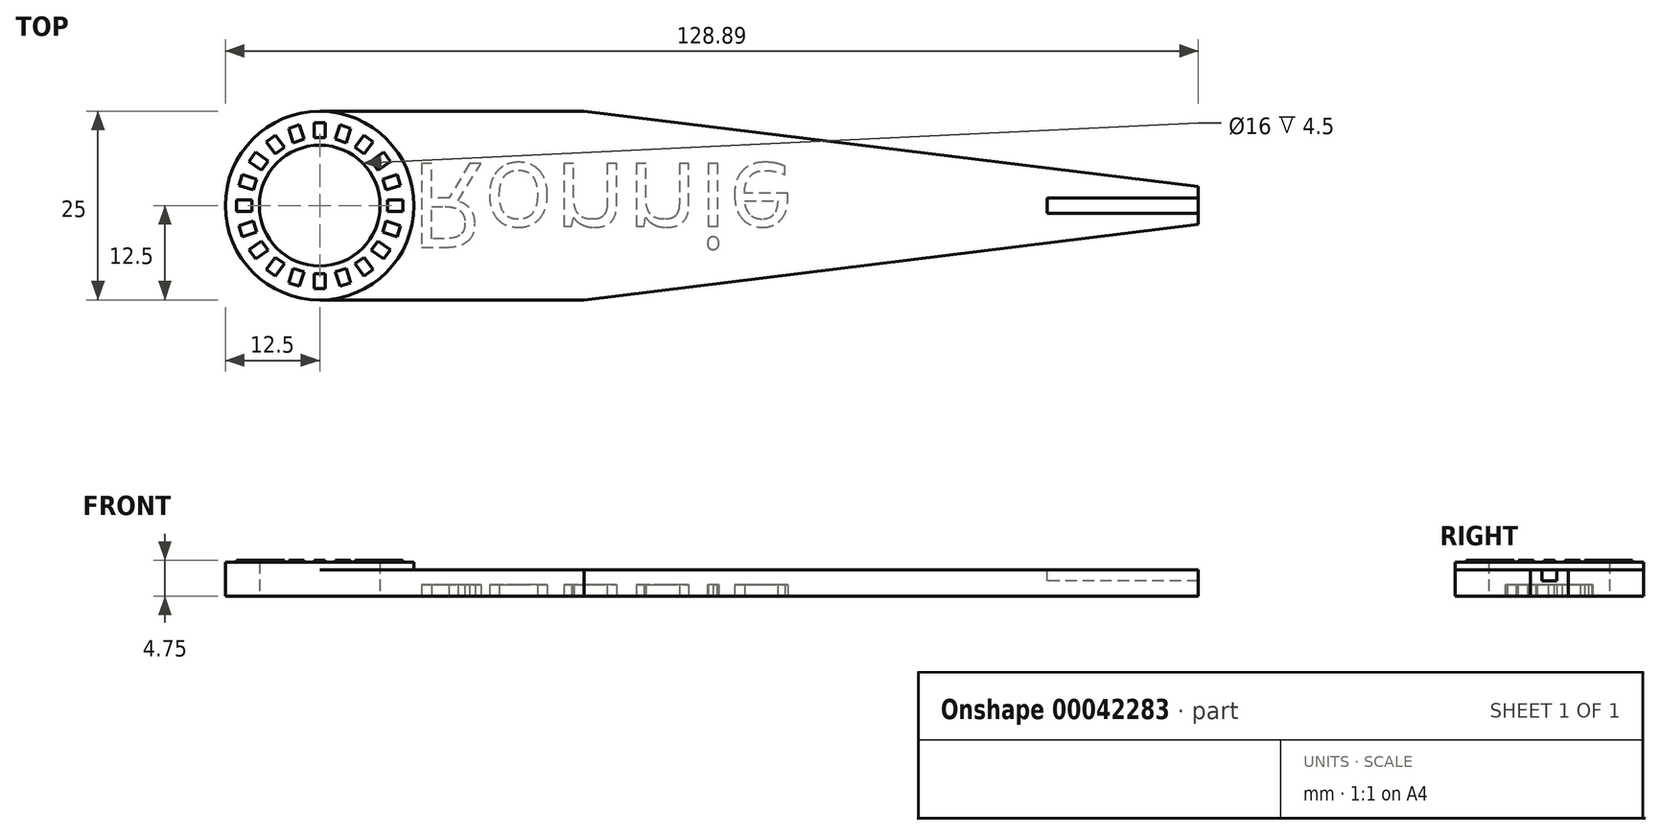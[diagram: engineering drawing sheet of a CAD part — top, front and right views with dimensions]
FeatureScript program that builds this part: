
annotation { "Feature Type Name" : "Feature", "Feature Type Description" : "" }
export const myFeature = defineFeature(function(context is Context, id is Id, definition is map)
    precondition{}
    {
        {
            var Q0;
            Q0=qCreatedBy(makeId("Top.planeOp"),FACE);
            var sketch = newSketch(context, id + "F0", { "sketchPlane" : qUnion([Q0])});
            skArc(sketch, "E0", {"start": v(0, 12.5) * mm, "mid": v(-12.5, 0) * mm, "end": v(0, -12.5) * mm});
            skCircle(sketch, "E1", {"center": v(0, 0) * mm, "radius": 8 * mm});
            skLineSegment(sketch, "E2", {"start": v(0, 12.5) * mm, "end": v(35, 12.5) * mm});
            skLineSegment(sketch, "E3", {"start": v(35, 12.5) * mm, "end": v(116.39, 2.5) * mm});
            skLineSegment(sketch, "E4", {"start": v(35, 12.5) * mm, "end": v(66.45, 12.5) * mm, "construction": true});
            skLineSegment(sketch, "E5", {"start": v(0, 0) * mm, "end": v(37.94, 0) * mm, "construction": true});
            skLineSegment(sketch, "E6.MirrorCS", {"start": v(0, -12.5) * mm, "end": v(35, -12.5) * mm});
            skLineSegment(sketch, "E7.MirrorCS", {"start": v(35, -12.5) * mm, "end": v(116.39, -2.5) * mm});
            skLineSegment(sketch, "E8", {"start": v(116.39, 2.5) * mm, "end": v(116.39, -2.5) * mm});
            skSolve(sketch);
        }
        {
            var Q0;
            Q0 = qSketchRegion(id + "F0", true);
            extrude(context, id + "F1", {"entities" : qUnion([Q0]), "depth" : 3.5 * mm});
        }
        {
            var Q0;
            Q0=makeQuery(id+"F1.opExtrude","CAP_FACE",FACE,{"disambiguationData":[OSD([sQuery(id+"F0.wireOp",EDGE,"E0"),sQuery(id+"F0.wireOp",EDGE,"E1"),sQuery(id+"F0.wireOp",EDGE,"E2"),sQuery(id+"F0.wireOp",EDGE,"E3"),sQuery(id+"F0.wireOp",EDGE,"E6.MirrorCS"),sQuery(id+"F0.wireOp",EDGE,"E7.MirrorCS"),sQuery(id+"F0.wireOp",EDGE,"E8")])],"isStart":false});
            var sketch = newSketch(context, id + "F2", { "sketchPlane" : qUnion([Q0])});
            skCircle(sketch, "E9", {"center": v(0, 0) * mm, "radius": 12.5 * mm});
            skCircle(sketch, "E10", {"center": v(0, 0) * mm, "radius": 8 * mm});
            skSolve(sketch);
        }
        {
            var Q0;
            Q0 = qSketchRegion(id + "F2", true);
            extrude(context, id + "F3", {"entities" : qUnion([Q0]), "operationType" : NewBodyOperationType.ADD, "depth" : 1 * mm});
        }
        {
            var Q0;
            Q0=makeQuery(id+"F3.opExtrude","CAP_FACE",FACE,{"disambiguationData":[OSD([sQuery(id+"F2.wireOp",EDGE,"E9"),sQuery(id+"F2.wireOp",EDGE,"E10")])],"isStart":false});
            var sketch = newSketch(context, id + "F4", { "sketchPlane" : qUnion([Q0])});
            skLineSegment(sketch, "E11.bottom", {"start": v(-0.75, 11) * mm, "end": v(0.75, 11) * mm});
            skLineSegment(sketch, "E11.top", {"start": v(-0.75, 9) * mm, "end": v(0.75, 9) * mm});
            skLineSegment(sketch, "E11.left", {"start": v(-0.75, 11) * mm, "end": v(-0.75, 9) * mm});
            skLineSegment(sketch, "E11.right", {"start": v(0.75, 11) * mm, "end": v(0.75, 9) * mm});
            skLineSegment(sketch, "E12.1.0", {"start": v(-4.11, 10.23) * mm, "end": v(-3.5, 8.33) * mm});
            skLineSegment(sketch, "E12.1.1", {"start": v(-4.11, 10.23) * mm, "end": v(-2.69, 10.7) * mm});
            skLineSegment(sketch, "E12.1.2", {"start": v(-2.69, 10.7) * mm, "end": v(-2.07, 8.8) * mm});
            skLineSegment(sketch, "E12.1.3", {"start": v(-3.5, 8.33) * mm, "end": v(-2.07, 8.8) * mm});
            skLineSegment(sketch, "E12.2.0", {"start": v(-7.07, 8.46) * mm, "end": v(-5.9, 6.84) * mm});
            skLineSegment(sketch, "E12.2.1", {"start": v(-7.07, 8.46) * mm, "end": v(-5.86, 9.34) * mm});
            skLineSegment(sketch, "E12.2.2", {"start": v(-5.86, 9.34) * mm, "end": v(-4.68, 7.72) * mm});
            skLineSegment(sketch, "E12.2.3", {"start": v(-5.9, 6.84) * mm, "end": v(-4.68, 7.72) * mm});
            skLineSegment(sketch, "E12.3.0", {"start": v(-9.34, 5.86) * mm, "end": v(-7.72, 4.68) * mm});
            skLineSegment(sketch, "E12.3.1", {"start": v(-9.34, 5.86) * mm, "end": v(-8.46, 7.07) * mm});
            skLineSegment(sketch, "E12.3.2", {"start": v(-8.46, 7.07) * mm, "end": v(-6.84, 5.9) * mm});
            skLineSegment(sketch, "E12.3.3", {"start": v(-7.72, 4.68) * mm, "end": v(-6.84, 5.9) * mm});
            skLineSegment(sketch, "E12.4.0", {"start": v(-10.7, 2.69) * mm, "end": v(-8.8, 2.07) * mm});
            skLineSegment(sketch, "E12.4.1", {"start": v(-10.7, 2.69) * mm, "end": v(-10.23, 4.11) * mm});
            skLineSegment(sketch, "E12.4.2", {"start": v(-10.23, 4.11) * mm, "end": v(-8.33, 3.5) * mm});
            skLineSegment(sketch, "E12.4.3", {"start": v(-8.8, 2.07) * mm, "end": v(-8.33, 3.5) * mm});
            skLineSegment(sketch, "E12.5.0", {"start": v(-11, -0.75) * mm, "end": v(-9, -0.75) * mm});
            skLineSegment(sketch, "E12.5.1", {"start": v(-11, -0.75) * mm, "end": v(-11, 0.75) * mm});
            skLineSegment(sketch, "E12.5.2", {"start": v(-11, 0.75) * mm, "end": v(-9, 0.75) * mm});
            skLineSegment(sketch, "E12.5.3", {"start": v(-9, -0.75) * mm, "end": v(-9, 0.75) * mm});
            skLineSegment(sketch, "E12.6.0", {"start": v(-10.23, -4.11) * mm, "end": v(-8.33, -3.5) * mm});
            skLineSegment(sketch, "E12.6.1", {"start": v(-10.23, -4.11) * mm, "end": v(-10.7, -2.69) * mm});
            skLineSegment(sketch, "E12.6.2", {"start": v(-10.7, -2.69) * mm, "end": v(-8.8, -2.07) * mm});
            skLineSegment(sketch, "E12.6.3", {"start": v(-8.33, -3.5) * mm, "end": v(-8.8, -2.07) * mm});
            skLineSegment(sketch, "E12.7.0", {"start": v(-8.46, -7.07) * mm, "end": v(-6.84, -5.9) * mm});
            skLineSegment(sketch, "E12.7.1", {"start": v(-8.46, -7.07) * mm, "end": v(-9.34, -5.86) * mm});
            skLineSegment(sketch, "E12.7.2", {"start": v(-9.34, -5.86) * mm, "end": v(-7.72, -4.68) * mm});
            skLineSegment(sketch, "E12.7.3", {"start": v(-6.84, -5.9) * mm, "end": v(-7.72, -4.68) * mm});
            skLineSegment(sketch, "E12.8.0", {"start": v(-5.86, -9.34) * mm, "end": v(-4.68, -7.72) * mm});
            skLineSegment(sketch, "E12.8.1", {"start": v(-5.86, -9.34) * mm, "end": v(-7.07, -8.46) * mm});
            skLineSegment(sketch, "E12.8.2", {"start": v(-7.07, -8.46) * mm, "end": v(-5.9, -6.84) * mm});
            skLineSegment(sketch, "E12.8.3", {"start": v(-4.68, -7.72) * mm, "end": v(-5.9, -6.84) * mm});
            skLineSegment(sketch, "E12.9.0", {"start": v(-2.69, -10.7) * mm, "end": v(-2.07, -8.8) * mm});
            skLineSegment(sketch, "E12.9.1", {"start": v(-2.69, -10.7) * mm, "end": v(-4.11, -10.23) * mm});
            skLineSegment(sketch, "E12.9.2", {"start": v(-4.11, -10.23) * mm, "end": v(-3.5, -8.33) * mm});
            skLineSegment(sketch, "E12.9.3", {"start": v(-2.07, -8.8) * mm, "end": v(-3.5, -8.33) * mm});
            skLineSegment(sketch, "E12.10.0", {"start": v(0.75, -11) * mm, "end": v(0.75, -9) * mm});
            skLineSegment(sketch, "E12.10.1", {"start": v(0.75, -11) * mm, "end": v(-0.75, -11) * mm});
            skLineSegment(sketch, "E12.10.2", {"start": v(-0.75, -11) * mm, "end": v(-0.75, -9) * mm});
            skLineSegment(sketch, "E12.10.3", {"start": v(0.75, -9) * mm, "end": v(-0.75, -9) * mm});
            skLineSegment(sketch, "E12.11.0", {"start": v(4.11, -10.23) * mm, "end": v(3.5, -8.33) * mm});
            skLineSegment(sketch, "E12.11.1", {"start": v(4.11, -10.23) * mm, "end": v(2.69, -10.7) * mm});
            skLineSegment(sketch, "E12.11.2", {"start": v(2.69, -10.7) * mm, "end": v(2.07, -8.8) * mm});
            skLineSegment(sketch, "E12.11.3", {"start": v(3.5, -8.33) * mm, "end": v(2.07, -8.8) * mm});
            skLineSegment(sketch, "E12.12.0", {"start": v(7.07, -8.46) * mm, "end": v(5.9, -6.84) * mm});
            skLineSegment(sketch, "E12.12.1", {"start": v(7.07, -8.46) * mm, "end": v(5.86, -9.34) * mm});
            skLineSegment(sketch, "E12.12.2", {"start": v(5.86, -9.34) * mm, "end": v(4.68, -7.72) * mm});
            skLineSegment(sketch, "E12.12.3", {"start": v(5.9, -6.84) * mm, "end": v(4.68, -7.72) * mm});
            skLineSegment(sketch, "E12.13.0", {"start": v(9.34, -5.86) * mm, "end": v(7.72, -4.68) * mm});
            skLineSegment(sketch, "E12.13.1", {"start": v(9.34, -5.86) * mm, "end": v(8.46, -7.07) * mm});
            skLineSegment(sketch, "E12.13.2", {"start": v(8.46, -7.07) * mm, "end": v(6.84, -5.9) * mm});
            skLineSegment(sketch, "E12.13.3", {"start": v(7.72, -4.68) * mm, "end": v(6.84, -5.9) * mm});
            skLineSegment(sketch, "E12.14.0", {"start": v(10.7, -2.69) * mm, "end": v(8.8, -2.07) * mm});
            skLineSegment(sketch, "E12.14.1", {"start": v(10.7, -2.69) * mm, "end": v(10.23, -4.11) * mm});
            skLineSegment(sketch, "E12.14.2", {"start": v(10.23, -4.11) * mm, "end": v(8.33, -3.5) * mm});
            skLineSegment(sketch, "E12.14.3", {"start": v(8.8, -2.07) * mm, "end": v(8.33, -3.5) * mm});
            skLineSegment(sketch, "E12.15.0", {"start": v(11, 0.75) * mm, "end": v(9, 0.75) * mm});
            skLineSegment(sketch, "E12.15.1", {"start": v(11, 0.75) * mm, "end": v(11, -0.75) * mm});
            skLineSegment(sketch, "E12.15.2", {"start": v(11, -0.75) * mm, "end": v(9, -0.75) * mm});
            skLineSegment(sketch, "E12.15.3", {"start": v(9, 0.75) * mm, "end": v(9, -0.75) * mm});
            skLineSegment(sketch, "E12.16.0", {"start": v(10.23, 4.11) * mm, "end": v(8.33, 3.5) * mm});
            skLineSegment(sketch, "E12.16.1", {"start": v(10.23, 4.11) * mm, "end": v(10.7, 2.69) * mm});
            skLineSegment(sketch, "E12.16.2", {"start": v(10.7, 2.69) * mm, "end": v(8.8, 2.07) * mm});
            skLineSegment(sketch, "E12.16.3", {"start": v(8.33, 3.5) * mm, "end": v(8.8, 2.07) * mm});
            skLineSegment(sketch, "E12.17.0", {"start": v(8.46, 7.07) * mm, "end": v(6.84, 5.9) * mm});
            skLineSegment(sketch, "E12.17.1", {"start": v(8.46, 7.07) * mm, "end": v(9.34, 5.86) * mm});
            skLineSegment(sketch, "E12.17.2", {"start": v(9.34, 5.86) * mm, "end": v(7.72, 4.68) * mm});
            skLineSegment(sketch, "E12.17.3", {"start": v(6.84, 5.9) * mm, "end": v(7.72, 4.68) * mm});
            skLineSegment(sketch, "E12.18.0", {"start": v(5.86, 9.34) * mm, "end": v(4.68, 7.72) * mm});
            skLineSegment(sketch, "E12.18.1", {"start": v(5.86, 9.34) * mm, "end": v(7.07, 8.46) * mm});
            skLineSegment(sketch, "E12.18.2", {"start": v(7.07, 8.46) * mm, "end": v(5.9, 6.84) * mm});
            skLineSegment(sketch, "E12.18.3", {"start": v(4.68, 7.72) * mm, "end": v(5.9, 6.84) * mm});
            skLineSegment(sketch, "E12.19.0", {"start": v(2.69, 10.7) * mm, "end": v(2.07, 8.8) * mm});
            skLineSegment(sketch, "E12.19.1", {"start": v(2.69, 10.7) * mm, "end": v(4.11, 10.23) * mm});
            skLineSegment(sketch, "E12.19.2", {"start": v(4.11, 10.23) * mm, "end": v(3.5, 8.33) * mm});
            skLineSegment(sketch, "E12.19.3", {"start": v(2.07, 8.8) * mm, "end": v(3.5, 8.33) * mm});
            skPoint(sketch, "E12.center", {"position": v(0, 0) * mm});
            skSolve(sketch);
        }
        {
            var Q0;
            Q0 = qSketchRegion(id + "F4", true);
            extrude(context, id + "F5", {"entities" : qUnion([Q0]), "operationType" : NewBodyOperationType.ADD, "depth" : .25 * mm});
        }
        {
            var Q0;
            Q0=makeQuery(id+"F1.opExtrude","CAP_FACE",FACE,{"disambiguationData":[OSD([sQuery(id+"F0.wireOp",EDGE,"E0"),sQuery(id+"F0.wireOp",EDGE,"E1"),sQuery(id+"F0.wireOp",EDGE,"E2"),sQuery(id+"F0.wireOp",EDGE,"E3"),sQuery(id+"F0.wireOp",EDGE,"E6.MirrorCS"),sQuery(id+"F0.wireOp",EDGE,"E7.MirrorCS"),sQuery(id+"F0.wireOp",EDGE,"E8")])],"isStart":false});
            var sketch = newSketch(context, id + "F6", { "sketchPlane" : qUnion([Q0])});
            skLineSegment(sketch, "E13.bottom", {"start": v(116.39, 1) * mm, "end": v(96.39, 1) * mm});
            skLineSegment(sketch, "E13.top", {"start": v(116.39, -1) * mm, "end": v(96.39, -1) * mm});
            skLineSegment(sketch, "E13.left", {"start": v(116.39, 1) * mm, "end": v(116.39, -1) * mm});
            skLineSegment(sketch, "E13.right", {"start": v(96.39, 1) * mm, "end": v(96.39, -1) * mm});
            skSolve(sketch);
        }
        {
            var Q0;
            Q0 = qSketchRegion(id + "F6", true);
            extrude(context, id + "F7", {"entities" : qUnion([Q0]), "operationType" : NewBodyOperationType.REMOVE, "oppositeDirection" : true, "depth" : 1.5 * mm});
        }
        {
            var Q0;
            Q0=qCreatedBy(makeId("Top.planeOp"),FACE);
            var Q1;
            Q1=makeQuery(id+"F1.opExtrude","CAP_EDGE",EDGE,{"disambiguationData":[OSD([sQuery(id+"F0.wireOp",EDGE,"E6.MirrorCS")])],"isStart":true});
            cPlane(context, id + "F8", {"entities" : qUnion([Q0, Q1]), "cplaneType" : CPlaneType.LINE_ANGLE, "offset" : 150 * mm, "angle" : 0 * degree, "width" : 150 * mm, "height" : 150 * mm});
        }
        {
            var Q0;
            Q0=qCreatedBy(id+"F8.planeOp",FACE);
            var sketch = newSketch(context, id + "F9", { "sketchPlane" : qUnion([Q0])});
            skText(sketch, "E14", { "text": "Ronnie", "fontName": "OpenSans-Regular.ttf"});
            skPoint(sketch, "E15", {"position": v(12, 0) * mm});
            skLineSegment(sketch, "E16", {"start": v(0, 0) * mm, "end": v(8.05, 0) * mm, "construction": true});
            const initialGuessF9  = {"E14": [0.012, -0.0056, 1, 0, 0.01121]};
            skSetInitialGuess(sketch, initialGuessF9);
            skSolve(sketch);
        }
        {
            var Q0;
            Q0 = qSketchRegion(id + "F9", true);
            extrude(context, id + "F10", {"entities" : qUnion([Q0]), "operationType" : NewBodyOperationType.REMOVE, "oppositeDirection" : true, "depth" : 1.5 * mm});
        }
    });
